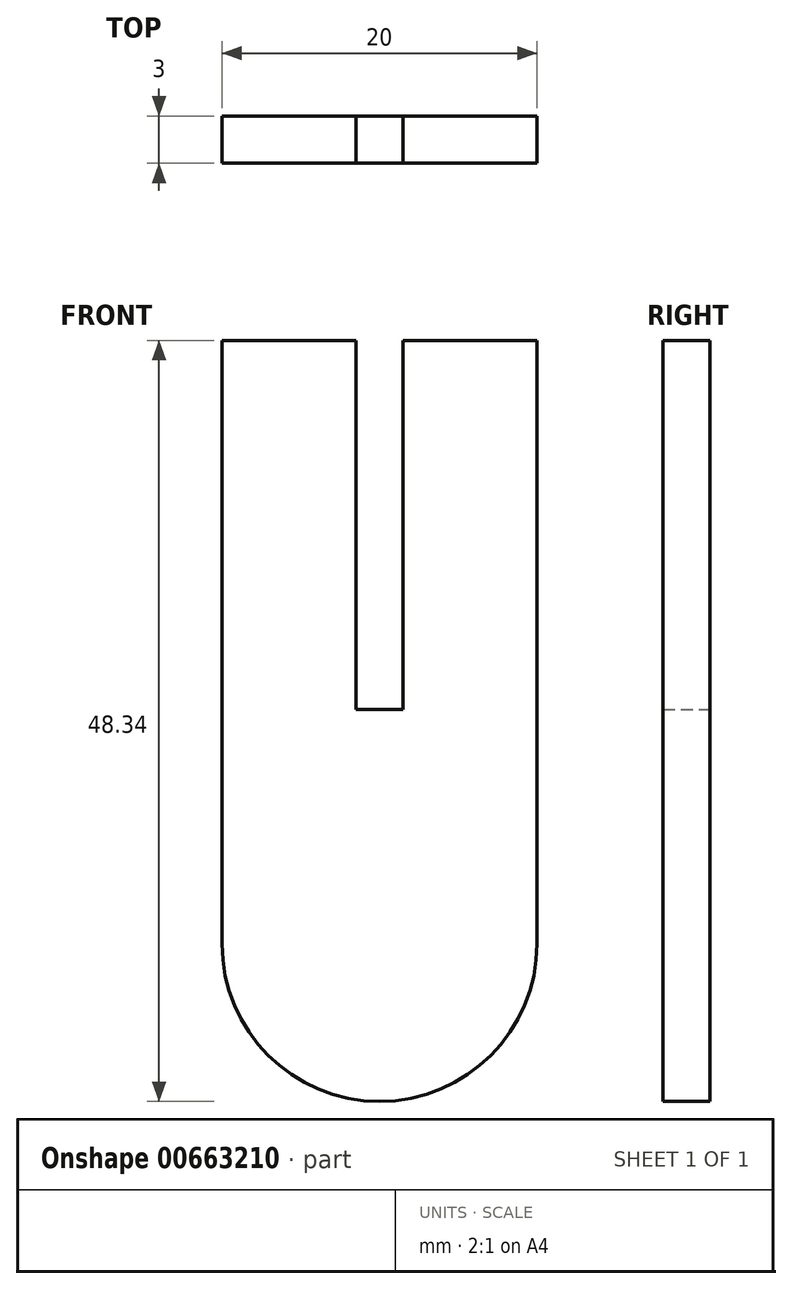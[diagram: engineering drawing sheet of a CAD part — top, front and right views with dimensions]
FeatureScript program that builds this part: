
annotation { "Feature Type Name" : "Feature", "Feature Type Description" : "" }
export const myFeature = defineFeature(function(context is Context, id is Id, definition is map)
    precondition{}
    {
        {
            var Q0;
            Q0=qCreatedBy(makeId("Front.planeOp"),FACE);
            var sketch = newSketch(context, id + "F0", { "sketchPlane" : qUnion([Q0])});
            skLineSegment(sketch, "E0", {"start": v(-10, 0) * mm, "end": v(-10, 38.34) * mm});
            skLineSegment(sketch, "E1", {"start": v(-10, 38.34) * mm, "end": v(-1.5, 38.34) * mm});
            skLineSegment(sketch, "E2", {"start": v(-1.5, 38.34) * mm, "end": v(-1.5, 14.9) * mm});
            skLineSegment(sketch, "E3", {"start": v(-1.5, 14.9) * mm, "end": v(1.5, 14.9) * mm});
            skLineSegment(sketch, "E4", {"start": v(1.5, 14.9) * mm, "end": v(1.5, 38.34) * mm});
            skLineSegment(sketch, "E5", {"start": v(1.5, 38.34) * mm, "end": v(10, 38.34) * mm});
            skLineSegment(sketch, "E6", {"start": v(10, 38.34) * mm, "end": v(10, 0) * mm});
            skArc(sketch, "E7", {"start": v(-10, 0) * mm, "mid": v(0, -10) * mm, "end": v(10, 0) * mm});
            skSolve(sketch);
        }
        {
            var Q0;
            Q0=qSketchRegion(id+"F0",true);
            extrude(context, id + "F1", {"entities" : qUnion([Q0]), "depth" : 3 * mm, "offsetDistance" : 25 * mm});
        }
    });
